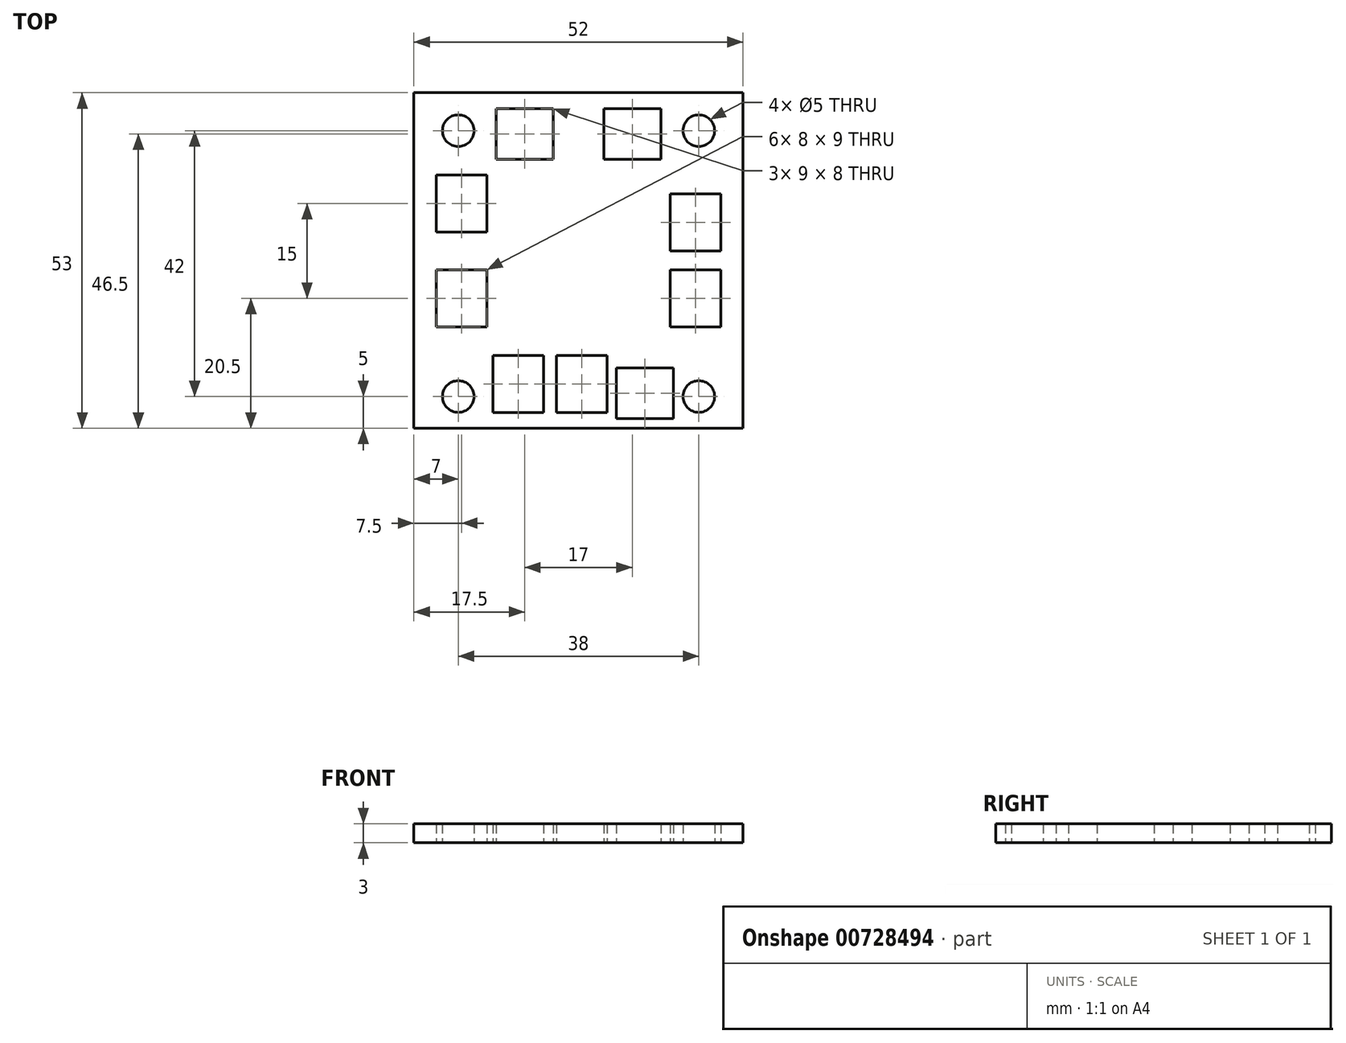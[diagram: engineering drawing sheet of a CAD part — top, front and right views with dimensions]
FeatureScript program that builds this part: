
annotation { "Feature Type Name" : "Feature", "Feature Type Description" : "" }
export const myFeature = defineFeature(function(context is Context, id is Id, definition is map)
    precondition{}
    {
        {
            var Q0;
            Q0=qCreatedBy(makeId("Top.planeOp"),FACE);
            var sketch = newSketch(context, id + "F0", { "sketchPlane" : qUnion([Q0])});
            skLineSegment(sketch, "E0.bottom", {"start": v(0, 0) * mm, "end": v(52, 0) * mm});
            skLineSegment(sketch, "E0.top", {"start": v(0, 53) * mm, "end": v(52, 53) * mm});
            skLineSegment(sketch, "E0.left", {"start": v(0, 0) * mm, "end": v(0, 53) * mm});
            skLineSegment(sketch, "E0.right", {"start": v(52, 0) * mm, "end": v(52, 53) * mm});
            skCircle(sketch, "E1", {"center": v(7, 5) * mm, "radius": 2.5 * mm});
            skCircle(sketch, "E2", {"center": v(7, 47) * mm, "radius": 2.5 * mm});
            skCircle(sketch, "E3", {"center": v(45, 47) * mm, "radius": 2.5 * mm});
            skCircle(sketch, "E4", {"center": v(45, 5) * mm, "radius": 2.5 * mm});
            skLineSegment(sketch, "E5.bottom", {"start": v(13, 50.5) * mm, "end": v(22, 50.5) * mm});
            skLineSegment(sketch, "E5.top", {"start": v(13, 42.5) * mm, "end": v(22, 42.5) * mm});
            skLineSegment(sketch, "E5.left", {"start": v(13, 50.5) * mm, "end": v(13, 42.5) * mm});
            skLineSegment(sketch, "E5.right", {"start": v(22, 50.5) * mm, "end": v(22, 42.5) * mm});
            skLineSegment(sketch, "E6.bottom", {"start": v(30, 50.5) * mm, "end": v(39, 50.5) * mm});
            skLineSegment(sketch, "E6.top", {"start": v(30, 42.5) * mm, "end": v(39, 42.5) * mm});
            skLineSegment(sketch, "E6.left", {"start": v(30, 50.5) * mm, "end": v(30, 42.5) * mm});
            skLineSegment(sketch, "E6.right", {"start": v(39, 50.5) * mm, "end": v(39, 42.5) * mm});
            skLineSegment(sketch, "E7.bottom", {"start": v(3.5, 40) * mm, "end": v(11.5, 40) * mm});
            skLineSegment(sketch, "E7.top", {"start": v(3.5, 31) * mm, "end": v(11.5, 31) * mm});
            skLineSegment(sketch, "E7.left", {"start": v(3.5, 40) * mm, "end": v(3.5, 31) * mm});
            skLineSegment(sketch, "E7.right", {"start": v(11.5, 40) * mm, "end": v(11.5, 31) * mm});
            skLineSegment(sketch, "E8.bottom", {"start": v(3.5, 25) * mm, "end": v(11.5, 25) * mm});
            skLineSegment(sketch, "E8.top", {"start": v(3.5, 16) * mm, "end": v(11.5, 16) * mm});
            skLineSegment(sketch, "E8.left", {"start": v(3.5, 25) * mm, "end": v(3.5, 16) * mm});
            skLineSegment(sketch, "E8.right", {"start": v(11.5, 25) * mm, "end": v(11.5, 16) * mm});
            skLineSegment(sketch, "E9.bottom", {"start": v(40.5, 37) * mm, "end": v(48.5, 37) * mm});
            skLineSegment(sketch, "E9.top", {"start": v(40.5, 28) * mm, "end": v(48.5, 28) * mm});
            skLineSegment(sketch, "E9.left", {"start": v(40.5, 37) * mm, "end": v(40.5, 28) * mm});
            skLineSegment(sketch, "E9.right", {"start": v(48.5, 37) * mm, "end": v(48.5, 28) * mm});
            skLineSegment(sketch, "E10.bottom", {"start": v(40.5, 25) * mm, "end": v(48.5, 25) * mm});
            skLineSegment(sketch, "E10.top", {"start": v(40.5, 16) * mm, "end": v(48.5, 16) * mm});
            skLineSegment(sketch, "E10.left", {"start": v(40.5, 25) * mm, "end": v(40.5, 16) * mm});
            skLineSegment(sketch, "E10.right", {"start": v(48.5, 25) * mm, "end": v(48.5, 16) * mm});
            skLineSegment(sketch, "E11.bottom", {"start": v(12.5, 11.5) * mm, "end": v(20.5, 11.5) * mm});
            skLineSegment(sketch, "E11.top", {"start": v(12.5, 2.5) * mm, "end": v(20.5, 2.5) * mm});
            skLineSegment(sketch, "E11.left", {"start": v(12.5, 11.5) * mm, "end": v(12.5, 2.5) * mm});
            skLineSegment(sketch, "E11.right", {"start": v(20.5, 11.5) * mm, "end": v(20.5, 2.5) * mm});
            skLineSegment(sketch, "E12.bottom", {"start": v(22.5, 11.5) * mm, "end": v(30.5, 11.5) * mm});
            skLineSegment(sketch, "E12.top", {"start": v(22.5, 2.5) * mm, "end": v(30.5, 2.5) * mm});
            skLineSegment(sketch, "E12.left", {"start": v(22.5, 11.5) * mm, "end": v(22.5, 2.5) * mm});
            skLineSegment(sketch, "E12.right", {"start": v(30.5, 11.5) * mm, "end": v(30.5, 2.5) * mm});
            skLineSegment(sketch, "E13.bottom", {"start": v(32, 9.5) * mm, "end": v(41, 9.5) * mm});
            skLineSegment(sketch, "E13.top", {"start": v(32, 1.5) * mm, "end": v(41, 1.5) * mm});
            skLineSegment(sketch, "E13.left", {"start": v(32, 9.5) * mm, "end": v(32, 1.5) * mm});
            skLineSegment(sketch, "E13.right", {"start": v(41, 9.5) * mm, "end": v(41, 1.5) * mm});
            skLineSegment(sketch, "E14", {"start": v(13, 46.5) * mm, "end": v(22, 46.5) * mm, "construction": true});
            skLineSegment(sketch, "E15", {"start": v(17.5, 50.5) * mm, "end": v(17.5, 42.5) * mm, "construction": true});
            skLineSegment(sketch, "E16", {"start": v(34.5, 50.5) * mm, "end": v(34.5, 42.5) * mm, "construction": true});
            skLineSegment(sketch, "E17", {"start": v(30, 46.5) * mm, "end": v(39, 46.5) * mm, "construction": true});
            skLineSegment(sketch, "E18", {"start": v(3.5, 35.5) * mm, "end": v(11.5, 35.5) * mm, "construction": true});
            skLineSegment(sketch, "E19", {"start": v(7.5, 40) * mm, "end": v(7.5, 31) * mm, "construction": true});
            skLineSegment(sketch, "E20", {"start": v(7.5, 25) * mm, "end": v(7.5, 16) * mm, "construction": true});
            skLineSegment(sketch, "E21", {"start": v(3.5, 20.5) * mm, "end": v(11.5, 20.5) * mm, "construction": true});
            skLineSegment(sketch, "E22", {"start": v(44.5, 37) * mm, "end": v(44.5, 28) * mm, "construction": true});
            skLineSegment(sketch, "E23", {"start": v(44.5, 28) * mm, "end": v(44.5, 37) * mm, "construction": true});
            skLineSegment(sketch, "E24", {"start": v(40.5, 32.5) * mm, "end": v(48.5, 32.5) * mm, "construction": true});
            skLineSegment(sketch, "E25", {"start": v(44.5, 25) * mm, "end": v(44.5, 16) * mm, "construction": true});
            skLineSegment(sketch, "E26", {"start": v(40.5, 20.5) * mm, "end": v(48.5, 20.5) * mm, "construction": true});
            skLineSegment(sketch, "E27", {"start": v(16.5, 11.5) * mm, "end": v(16.5, 2.5) * mm, "construction": true});
            skLineSegment(sketch, "E28", {"start": v(12.5, 7) * mm, "end": v(20.5, 7) * mm, "construction": true});
            skLineSegment(sketch, "E29", {"start": v(22.5, 7) * mm, "end": v(30.5, 7) * mm, "construction": true});
            skLineSegment(sketch, "E30", {"start": v(26.5, 11.5) * mm, "end": v(26.5, 2.5) * mm, "construction": true});
            skLineSegment(sketch, "E31", {"start": v(36.5, 9.5) * mm, "end": v(36.5, 1.5) * mm, "construction": true});
            skLineSegment(sketch, "E32", {"start": v(32, 5.5) * mm, "end": v(41, 5.5) * mm, "construction": true});
            skSolve(sketch);
        }
        {
            var Q0;
            Q0=makeQuery(id+"F0.imprint","IMPRINT",FACE,{"disambiguationData":[TD([[makeQuery(id+"F0.imprint","IMPRINT",EDGE,{"derivedFrom":sQuery(id+"F0.wireOp",EDGE,"E0.bottom")}),1.0]])]});
            extrude(context, id + "F1", {"entities" : qUnion([Q0]), "depth" : 3 * mm, "offsetDistance" : 25 * mm});
        }
    });
